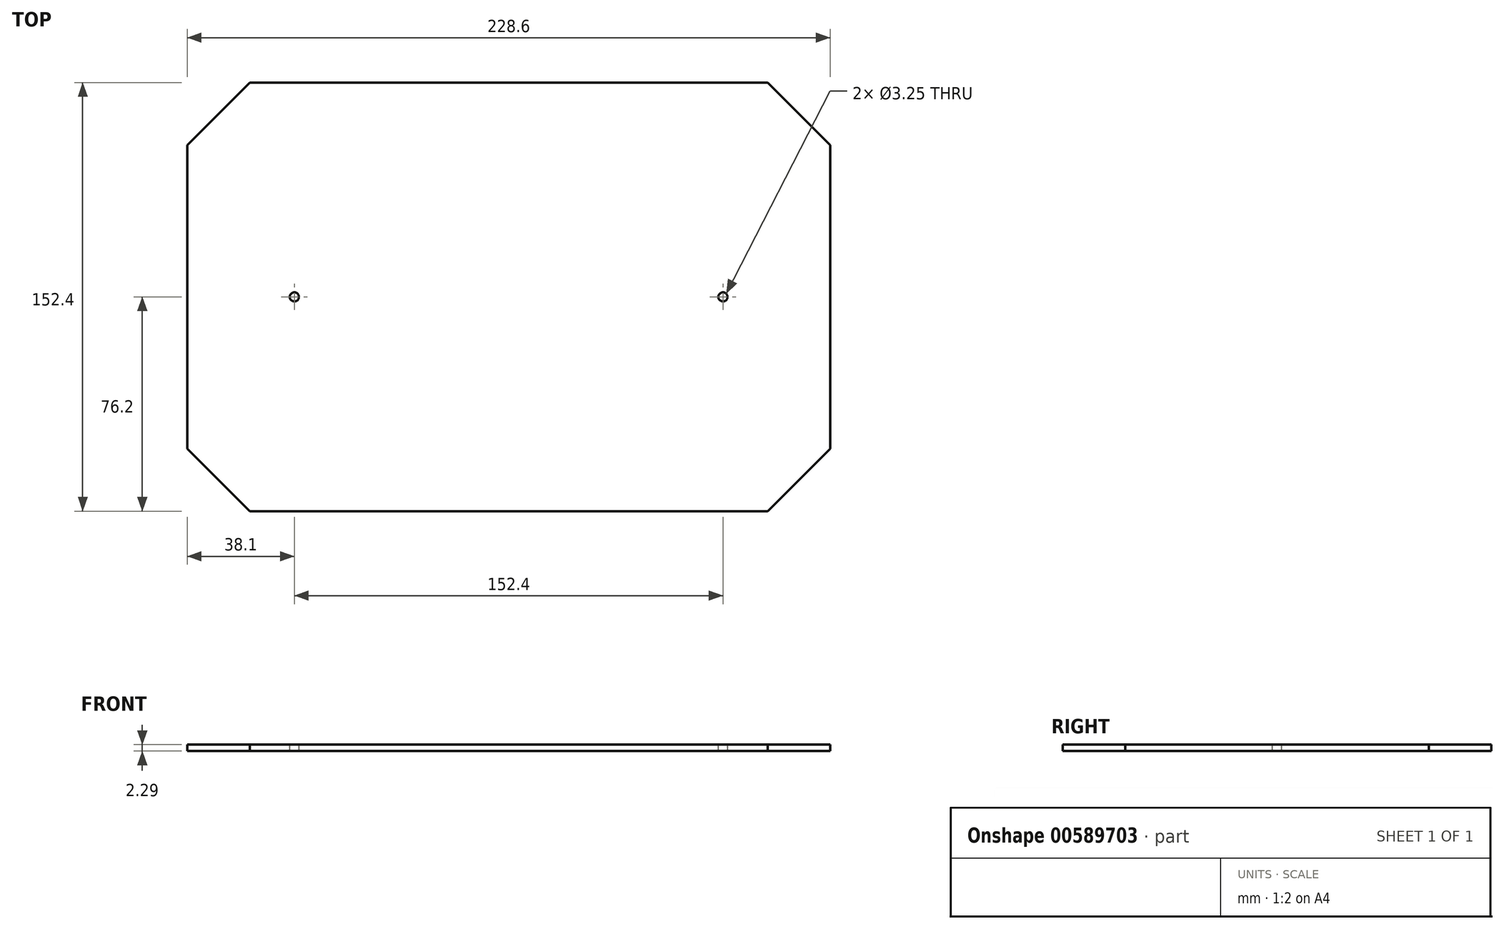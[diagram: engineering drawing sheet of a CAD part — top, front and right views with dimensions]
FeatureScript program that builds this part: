
annotation { "Feature Type Name" : "Feature", "Feature Type Description" : "" }
export const myFeature = defineFeature(function(context is Context, id is Id, definition is map)
    precondition{}
    {
        {
            var Q0;
            Q0=qCreatedBy(makeId("Top.planeOp"),FACE);
            var sketch = newSketch(context, id + "F0", { "sketchPlane" : qUnion([Q0])});
            skLineSegment(sketch, "E0.bottom", {"start": v(-114.3, -76.2) * mm, "end": v(114.3, -76.2) * mm});
            skLineSegment(sketch, "E0.top", {"start": v(-114.3, 76.2) * mm, "end": v(114.3, 76.2) * mm});
            skLineSegment(sketch, "E0.left", {"start": v(-114.3, -76.2) * mm, "end": v(-114.3, 76.2) * mm});
            skLineSegment(sketch, "E0.right", {"start": v(114.3, -76.2) * mm, "end": v(114.3, 76.2) * mm});
            skPoint(sketch, "E0.middle", {"position": v(0, 0) * mm});
            skSolve(sketch);
        }
        {
            var Q0;
            Q0=makeQuery(id+"F0.imprint","IMPRINT",FACE,{"disambiguationData":[TD([[makeQuery(id+"F0.imprint","IMPRINT",EDGE,{"derivedFrom":sQuery(id+"F0.wireOp",EDGE,"E0.bottom")}),1.0]])]});
            extrude(context, id + "F1", {"entities" : qUnion([Q0]), "oppositeDirection" : true, "depth" : 2.3 * mm, "offsetDistance" : 25.4 * mm});
        }
        {
            var Q0;
            Q0=makeQuery(id+"F1.opExtrude","CAP_FACE",FACE,{"disambiguationData":[OSD([sQuery(id+"F0.wireOp",EDGE,"E0.bottom"),sQuery(id+"F0.wireOp",EDGE,"E0.top"),sQuery(id+"F0.wireOp",EDGE,"E0.left"),sQuery(id+"F0.wireOp",EDGE,"E0.right")])],"isStart":true});
            var sketch = newSketch(context, id + "F2", { "sketchPlane" : qUnion([Q0])});
            skLineSegment(sketch, "E1", {"start": v(0, 0) * mm, "end": v(-114.3, 0) * mm, "construction": true});
            skLineSegment(sketch, "E2", {"start": v(0, 0) * mm, "end": v(114.3, 0) * mm, "construction": true});
            skCircle(sketch, "E3", {"center": v(-76.2, 0) * mm, "radius": 1.63 * mm});
            skLineSegment(sketch, "E4", {"start": v(0, 76.2) * mm, "end": v(0, -76.2) * mm, "construction": true});
            skCircle(sketch, "E5.MirrorC", {"center": v(76.2, 0) * mm, "radius": 1.63 * mm});
            skSolve(sketch);
        }
        {
            var Q0;
            Q0 = qSketchRegion(id + "F2", true);
            extrude(context, id + "F3", {"entities" : qUnion([Q0]), "operationType" : NewBodyOperationType.REMOVE, "endBound" : BoundingType.THROUGH_ALL, "oppositeDirection" : true, "depth" : 25.4 * mm, "offsetDistance" : 25.4 * mm});
        }
        {
            var Q0;
            Q0=makeQuery(id+"F1.opExtrude","SWEPT_EDGE",EDGE,{"disambiguationData":[OSD([sQuery(id+"F0.wireOp",EDGE,"E0.top"),sQuery(id+"F0.wireOp",EDGE,"E0.left")])]});
            var Q1;
            Q1=makeQuery(id+"F1.opExtrude","SWEPT_EDGE",EDGE,{"disambiguationData":[OSD([sQuery(id+"F0.wireOp",EDGE,"E0.top"),sQuery(id+"F0.wireOp",EDGE,"E0.right")])]});
            var Q2;
            Q2=makeQuery(id+"F1.opExtrude","SWEPT_EDGE",EDGE,{"disambiguationData":[OSD([sQuery(id+"F0.wireOp",EDGE,"E0.bottom"),sQuery(id+"F0.wireOp",EDGE,"E0.left")])]});
            var Q3;
            Q3=makeQuery(id+"F1.opExtrude","SWEPT_EDGE",EDGE,{"disambiguationData":[OSD([sQuery(id+"F0.wireOp",EDGE,"E0.bottom"),sQuery(id+"F0.wireOp",EDGE,"E0.right")])]});
            chamfer(context, id + "F4", {"entities" : qUnion([Q0, Q1, Q2, Q3]), "width" : 22.22 * mm, "tangentPropagation" : true});
        }
    });
